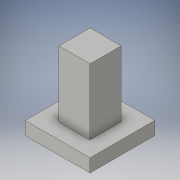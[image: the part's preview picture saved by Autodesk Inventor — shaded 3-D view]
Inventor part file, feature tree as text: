
AUTODESK INVENTOR PART (.ipt)
format: ipt  version: 2016 (Build 200138000, 138)  size: 98,304 bytes
history: native  units: in
note: dims shown in document units (in); Inventor stores cm internally (conversion verified against a paired STEP export)
features: extrude x2, sketch x2
ambient origin geometry x8: Origin, YZ Plane, XZ Plane, XY Plane, X Axis, Y Axis, Z Axis, Center Point
bodies: Solid1 (feature_tree)
feature tree (4):
  extrude  "Extrusion1"  Depth=9.8425in
  extrude  "Extrusion2"  Depth=4.7244in
  sketch  "Sketch1"  dims[d0=9.8425in d1=9.8425in]
  sketch  "Sketch2"  dims[d2=2.0in d3=0.0in d4=4.7244in d5=4.7244in d6=2.3622in d7=7.0866in d8=10.0in d9=0.0in]
